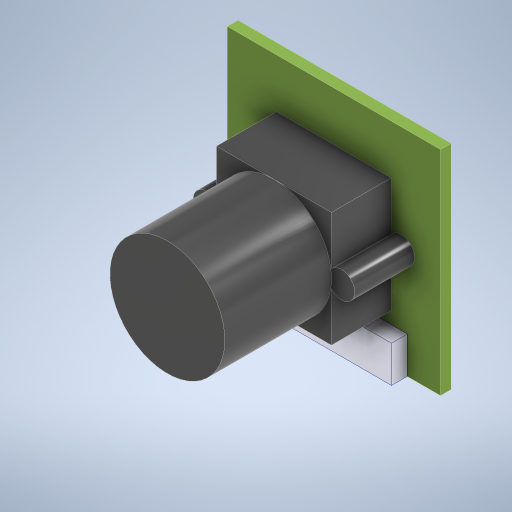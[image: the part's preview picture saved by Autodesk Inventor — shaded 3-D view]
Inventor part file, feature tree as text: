
AUTODESK INVENTOR PART (.ipt)
format: ipt  version: 2023 (Build 270158000, 158)  size: 287,744 bytes
history: native  units: mm
features: extrude x4, other x3, sketch x1
ambient origin geometry x8: Origin, YZ Plane, XZ Plane, XY Plane, X Axis, Y Axis, Z Axis, Center Point
bodies: Body1 (feature_tree), Body2 (feature_tree), Body3 (feature_tree)
feature tree (8):
  other  "Sólido1"
  sketch  "Boceto1"  dims[d0=32.0mm d1=22.0mm d2=5.5mm d3=17.25mm d4=4.0mm d6=1.5mm d7=1.5mm d8=9.0mm d9=0.0mm d10=1.61mm d11=0.0mm d12=2.35mm d13=0.0mm d14=25.0mm d15=0.0mm d16=13.625mm d17=2.0mm d18=1.0mm]
  extrude  "Extrusión1"  Depth=22.0mm
  extrude  "Extrusión2"  Depth=5.5mm
  extrude  "Extrusión3"  Depth=17.25mm
  extrude  "Extrusión4"  Depth=2.0mm
  other  "Sólido2"
  other  "Sólido3"
